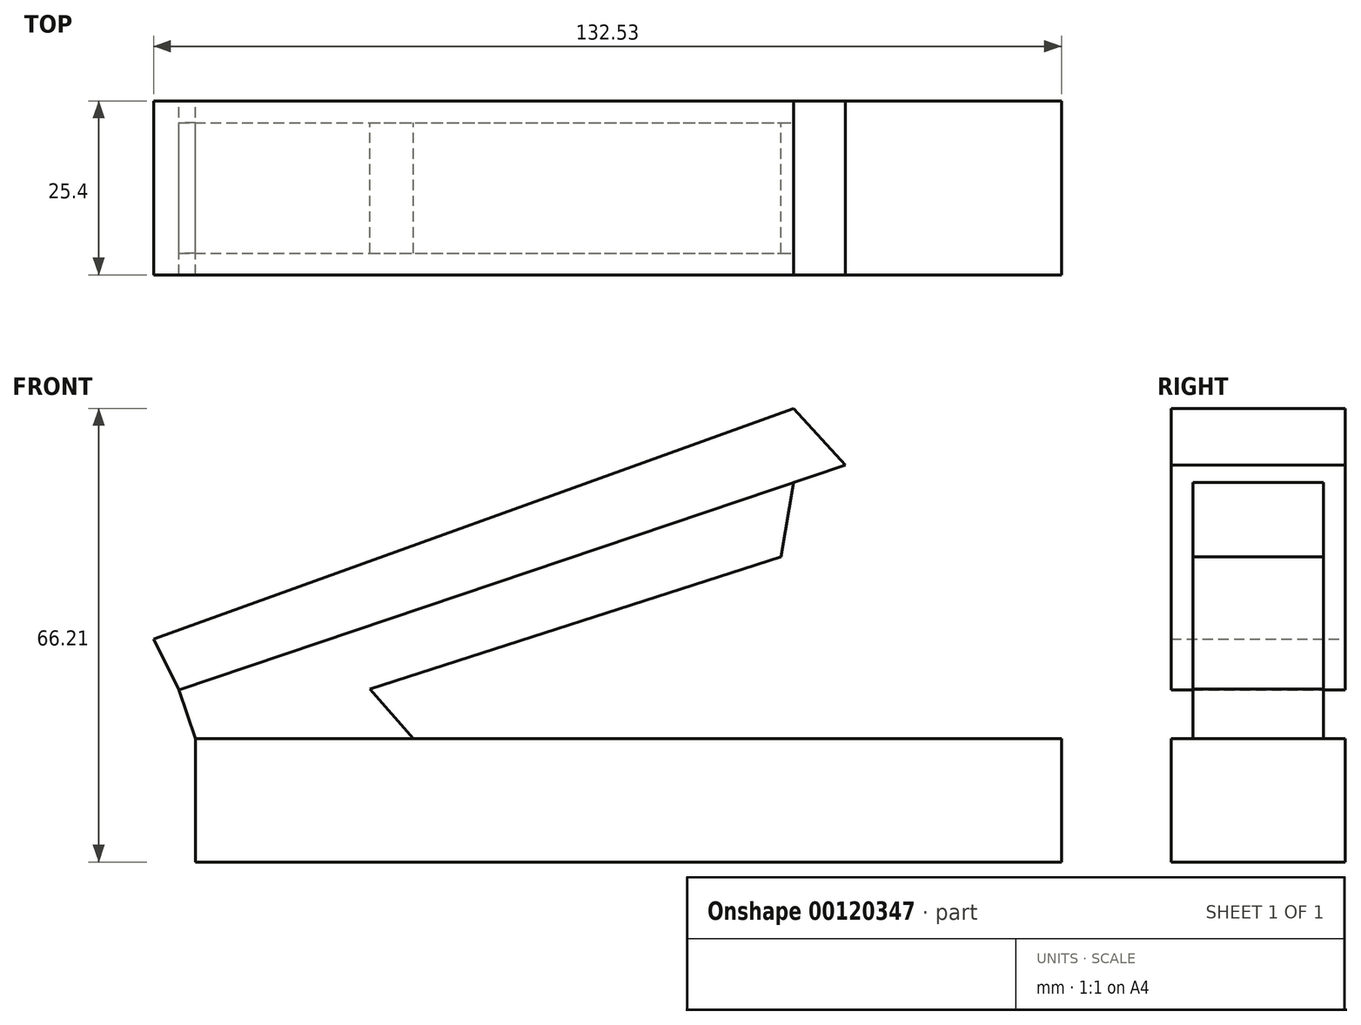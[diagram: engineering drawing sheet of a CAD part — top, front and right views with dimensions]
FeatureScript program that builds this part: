
annotation { "Feature Type Name" : "Feature", "Feature Type Description" : "" }
export const myFeature = defineFeature(function(context is Context, id is Id, definition is map)
    precondition{}
    {
        {
            var Q0;
            Q0=qCreatedBy(makeId("Front.planeOp"),FACE);
            var sketch = newSketch(context, id + "F0", { "sketchPlane" : qUnion([Q0])});
            skLineSegment(sketch, "E0.bottom", {"start": v(-63.22, 9.02) * mm, "end": v(63.22, 9.02) * mm});
            skLineSegment(sketch, "E0.top", {"start": v(-63.22, -9.02) * mm, "end": v(63.22, -9.02) * mm});
            skLineSegment(sketch, "E0.left", {"start": v(-63.22, 9.02) * mm, "end": v(-63.22, -9.02) * mm});
            skLineSegment(sketch, "E0.right", {"start": v(63.22, 9.02) * mm, "end": v(63.22, -9.02) * mm});
            skPoint(sketch, "E0.middle", {"position": v(0, 0) * mm});
            skLineSegment(sketch, "E1", {"start": v(-63.22, 9.02) * mm, "end": v(-65.6, 16.12) * mm});
            skLineSegment(sketch, "E2", {"start": v(-65.6, 16.12) * mm, "end": v(31.66, 48.92) * mm});
            skLineSegment(sketch, "E3", {"start": v(-44.07, 23.38) * mm, "end": v(-31.4, 9.02) * mm});
            skLineSegment(sketch, "E4", {"start": v(-37.74, 16.2) * mm, "end": v(22.25, 35.51) * mm});
            skLineSegment(sketch, "E5", {"start": v(22.25, 35.51) * mm, "end": v(24.14, 46.38) * mm});
            skLineSegment(sketch, "E6", {"start": v(31.66, 48.92) * mm, "end": v(24.14, 57.2) * mm});
            skLineSegment(sketch, "E7", {"start": v(24.14, 57.2) * mm, "end": v(-69.31, 23.53) * mm});
            skLineSegment(sketch, "E8", {"start": v(-69.31, 23.53) * mm, "end": v(-65.6, 16.12) * mm});
            skSolve(sketch);
        }
        {
            var Q0;
            {var subQ0=sQuery(id+"F0.wireOp",EDGE,"E6");Q0=makeQuery(id+"F0.imprint","IMPRINT",FACE,{"disambiguationData":[TD([[makeQuery(id+"F0.imprint","IMPRINT",EDGE,{"derivedFrom":subQ0}),1.0]])]});}
            var Q1;
            Q1=makeQuery(id+"F0.imprint","IMPRINT",FACE,{"disambiguationData":[TD([[makeQuery(id+"F0.imprint","IMPRINT",EDGE,{"derivedFrom":sQuery(id+"F0.wireOp",EDGE,"E0.top")}),1.0]])]});
            extrude(context, id + "F1", {"entities" : qUnion([Q0, Q1]), "endBound" : BoundingType.SYMMETRIC, "depth" : 25.4 * mm});
        }
        {
            var Q0;
            {var subQ4=sQuery(id+"F0.wireOp",EDGE,"E1");Q0=makeQuery(id+"F0.imprint","IMPRINT",FACE,{"disambiguationData":[TD([[makeQuery(id+"F0.imprint","IMPRINT",EDGE,{"derivedFrom":subQ4}),-1.0]])]});}
            var Q1;
            {var subQ4=sQuery(id+"F0.wireOp",EDGE,"E4");Q1=makeQuery(id+"F0.imprint","IMPRINT",FACE,{"disambiguationData":[TD([[makeQuery(id+"F0.imprint","IMPRINT",EDGE,{"derivedFrom":subQ4}),1.0]])]});}
            extrude(context, id + "F2", {"entities" : qUnion([Q0, Q1]), "endBound" : BoundingType.SYMMETRIC, "depth" : 19.05 * mm});
        }
    });
